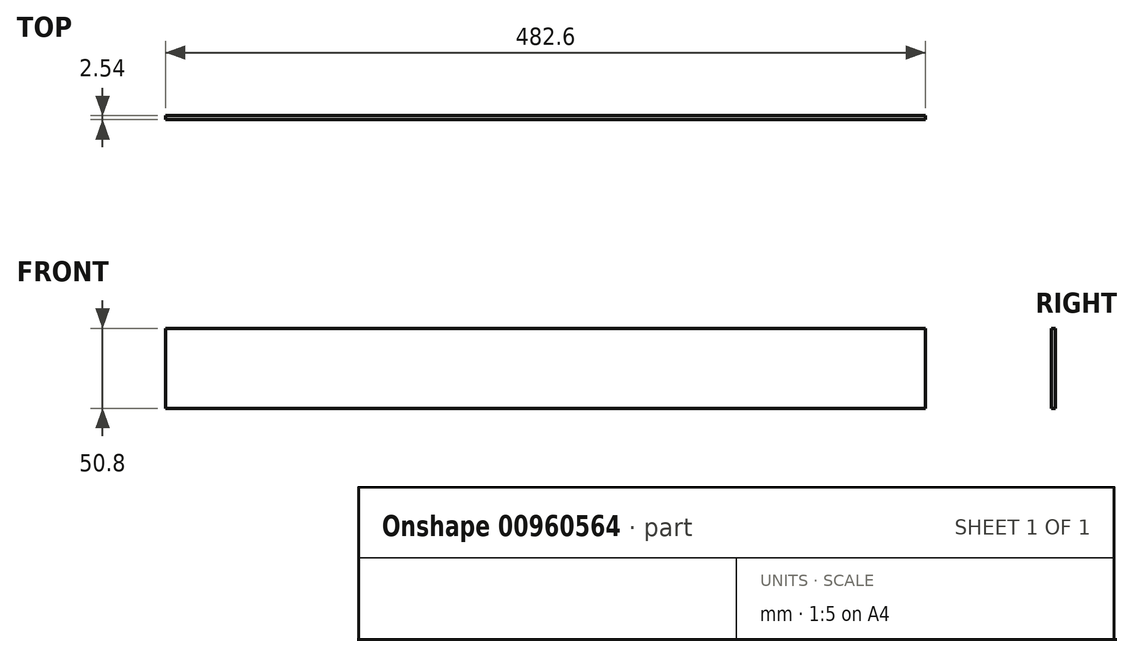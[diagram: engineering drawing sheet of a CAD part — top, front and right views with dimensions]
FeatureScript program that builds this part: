
annotation { "Feature Type Name" : "Feature", "Feature Type Description" : "" }
export const myFeature = defineFeature(function(context is Context, id is Id, definition is map)
    precondition{}
    {
        {
            var Q0;
            Q0=qCreatedBy(makeId("Front.planeOp"),FACE);
            var sketch = newSketch(context, id + "F0", { "sketchPlane" : qUnion([Q0])});
            skLineSegment(sketch, "E0.bottom", {"start": v(-265.8, 50.8) * mm, "end": v(216.8, 50.8) * mm});
            skLineSegment(sketch, "E0.top", {"start": v(-265.8, 0) * mm, "end": v(216.8, 0) * mm});
            skLineSegment(sketch, "E0.left", {"start": v(-265.8, 50.8) * mm, "end": v(-265.8, 0) * mm});
            skLineSegment(sketch, "E0.right", {"start": v(216.8, 50.8) * mm, "end": v(216.8, 0) * mm});
            skLineSegment(sketch, "E1", {"start": v(216.8, 0) * mm, "end": v(216.8, 50.8) * mm});
            skSolve(sketch);
        }
        {
            var Q0;
            Q0 = qSketchRegion(id + "F0", true);
            extrude(context, id + "F1", {"entities" : qUnion([Q0]), "depth" : 2.54 * mm, "offsetDistance" : 25.4 * mm});
        }
    });
